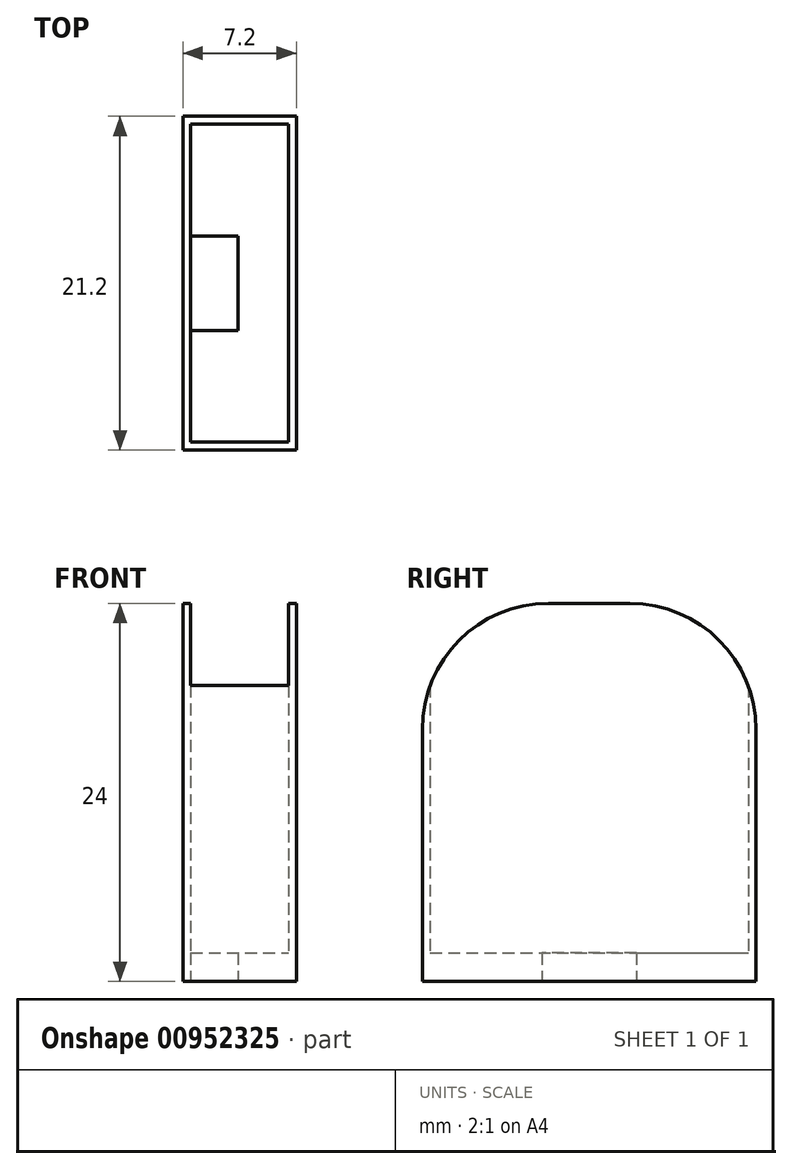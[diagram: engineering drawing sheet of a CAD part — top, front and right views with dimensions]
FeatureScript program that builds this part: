
annotation { "Feature Type Name" : "Feature", "Feature Type Description" : "" }
export const myFeature = defineFeature(function(context is Context, id is Id, definition is map)
    precondition{}
    {
        {
            var Q0;
            Q0=qCreatedBy(makeId("Top.planeOp"),FACE);
            var sketch = newSketch(context, id + "F0", { "sketchPlane" : qUnion([Q0])});
            skLineSegment(sketch, "E0.bottom", {"start": v(0, 0) * mm, "end": v(6.2, 0) * mm});
            skLineSegment(sketch, "E0.top", {"start": v(0, 20.2) * mm, "end": v(6.2, 20.2) * mm});
            skLineSegment(sketch, "E0.left", {"start": v(0, 0) * mm, "end": v(0, 20.2) * mm});
            skLineSegment(sketch, "E0.right", {"start": v(6.2, 0) * mm, "end": v(6.2, 20.2) * mm});
            skLineSegment(sketch, "E1.0", {"start": v(-0.5, 20.7) * mm, "end": v(6.7, 20.7) * mm});
            skLineSegment(sketch, "E1.1", {"start": v(-0.5, -0.5) * mm, "end": v(-0.5, 20.7) * mm});
            skLineSegment(sketch, "E1.2", {"start": v(-0.5, -0.5) * mm, "end": v(6.7, -0.5) * mm});
            skLineSegment(sketch, "E1.3", {"start": v(6.7, -0.5) * mm, "end": v(6.7, 20.7) * mm});
            skLineSegment(sketch, "E2", {"start": v(-0.5, 10.1) * mm, "end": v(6.7, 10.1) * mm, "construction": true});
            skLineSegment(sketch, "E3", {"start": v(0, 10.1) * mm, "end": v(0, 13.1) * mm});
            skLineSegment(sketch, "E4", {"start": v(0, 13.1) * mm, "end": v(3, 13.1) * mm});
            skLineSegment(sketch, "E5", {"start": v(3, 13.1) * mm, "end": v(3, 10.1) * mm});
            skLineSegment(sketch, "E6.MirrorCS", {"start": v(3, 7.1) * mm, "end": v(3, 10.1) * mm});
            skLineSegment(sketch, "E7.MirrorCS", {"start": v(0, 7.1) * mm, "end": v(3, 7.1) * mm});
            skSolve(sketch);
        }
        {
            var Q0;
            {var subQ3=sQuery(id+"F0.wireOp",EDGE,"E0.bottom");Q0=makeQuery(id+"F0.imprint","IMPRINT",FACE,{"disambiguationData":[TD([[makeQuery(id+"F0.imprint","IMPRINT",EDGE,{"derivedFrom":subQ3}),1.0]])]});}
            extrude(context, id + "F1", {"entities" : qUnion([Q0]), "depth" : 1.8 * mm, "offsetDistance" : 25 * mm});
        }
        {
            var Q0;
            {var subQ3=sQuery(id+"F0.wireOp",EDGE,"E0.bottom");Q0=makeQuery(id+"F0.imprint","IMPRINT",FACE,{"disambiguationData":[TD([[makeQuery(id+"F0.imprint","IMPRINT",EDGE,{"derivedFrom":subQ3}),-1.0]])]});}
            extrude(context, id + "F2", {"entities" : qUnion([Q0]), "operationType" : NewBodyOperationType.ADD, "depth" : 24 * mm, "offsetDistance" : 25 * mm});
        }
        {
            var Q0;
            Q0=makeQuery(id+"F2.opExtrude","CAP_EDGE",EDGE,{"disambiguationData":[OSD([sQuery(id+"F0.wireOp",EDGE,"E1.2")])],"isStart":false});
            var Q1;
            Q1=makeQuery(id+"F2.opExtrude","CAP_EDGE",EDGE,{"disambiguationData":[OSD([sQuery(id+"F0.wireOp",EDGE,"E1.0")])],"isStart":false});
            fillet(context, id + "F3", {"entities" : qUnion([Q0, Q1]), "radius" : 8 * mm, "tangentPropagation" : true, "allowEdgeOverflow" : false});
        }
    });
